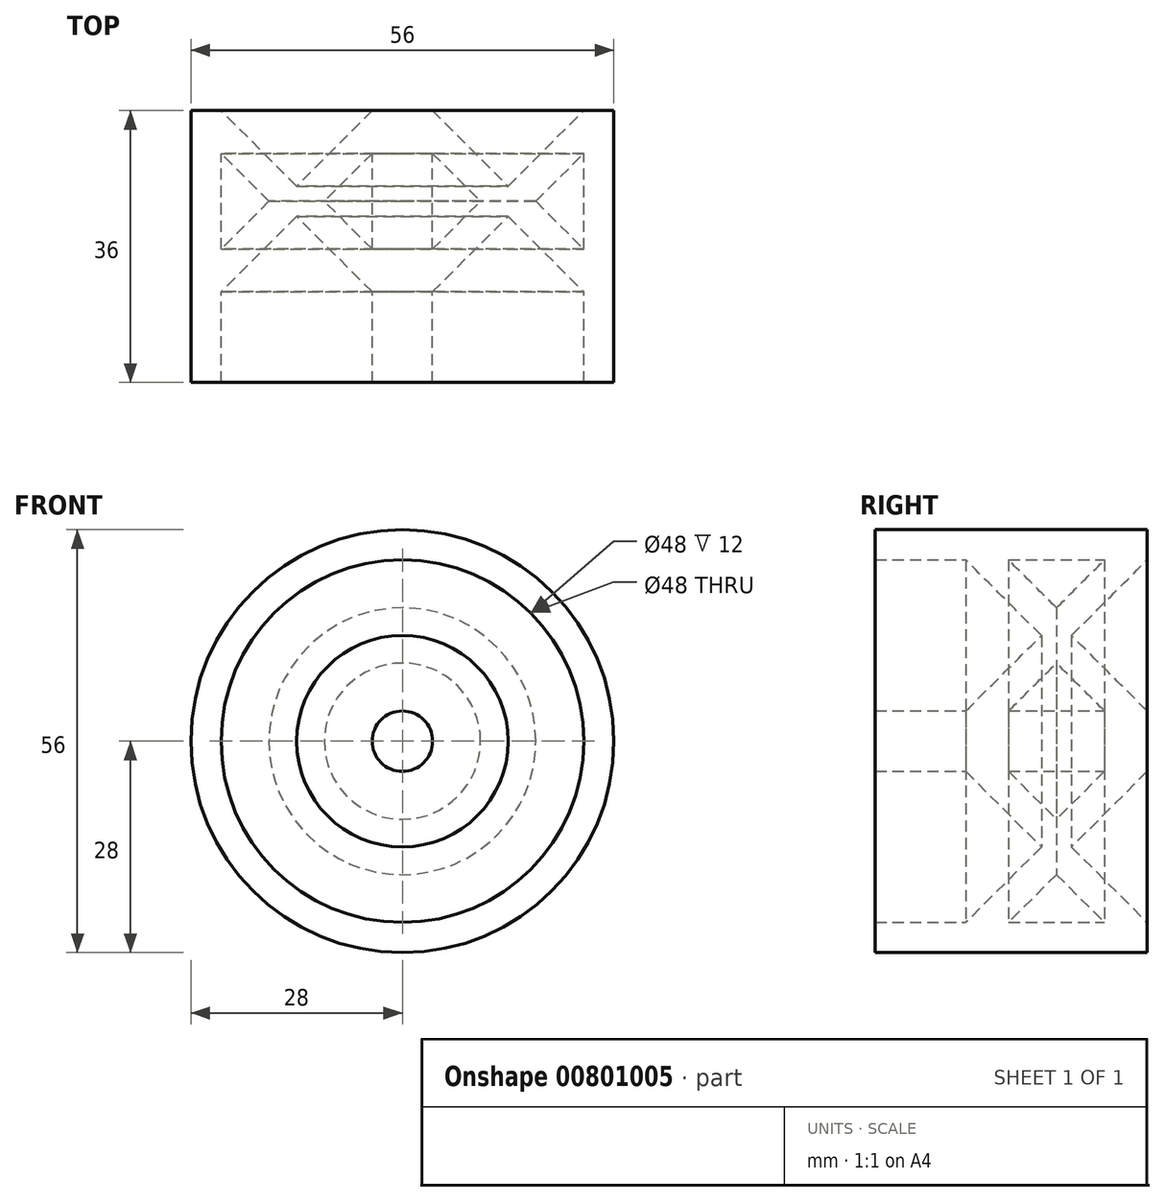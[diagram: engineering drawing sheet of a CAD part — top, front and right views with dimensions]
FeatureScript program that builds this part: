
annotation { "Feature Type Name" : "Feature", "Feature Type Description" : "" }
export const myFeature = defineFeature(function(context is Context, id is Id, definition is map)
    precondition{}
    {
        {
            var Q0;
            Q0=qCreatedBy(makeId("Top.planeOp"),FACE);
            var sketch = newSketch(context, id + "F0", { "sketchPlane" : qUnion([Q0])});
            skLineSegment(sketch, "E0", {"start": v(4, -24) * mm, "end": v(14, -14) * mm});
            skLineSegment(sketch, "E1", {"start": v(14, -14) * mm, "end": v(24, -24) * mm});
            skLineSegment(sketch, "E2", {"start": v(28, 0) * mm, "end": v(24, 0) * mm});
            skLineSegment(sketch, "E3", {"start": v(24, 0) * mm, "end": v(14, -10) * mm});
            skLineSegment(sketch, "E4", {"start": v(14, -10) * mm, "end": v(4, 0) * mm});
            skLineSegment(sketch, "E5", {"start": v(4, 0) * mm, "end": v(0, 0) * mm});
            skLineSegment(sketch, "E6", {"start": v(4, -18.34) * mm, "end": v(10.34, -12) * mm});
            skLineSegment(sketch, "E7", {"start": v(10.34, -12) * mm, "end": v(4, -5.66) * mm});
            skLineSegment(sketch, "E8", {"start": v(4, -5.66) * mm, "end": v(4, -18.34) * mm});
            skLineSegment(sketch, "E9", {"start": v(14, -10) * mm, "end": v(14, -14) * mm, "construction": true});
            skLineSegment(sketch, "E10.MirrorCS", {"start": v(17.66, -12) * mm, "end": v(24, -5.66) * mm});
            skLineSegment(sketch, "E11.MirrorCS", {"start": v(24, -5.66) * mm, "end": v(24, -18.34) * mm});
            skLineSegment(sketch, "E12.MirrorCS", {"start": v(24, -18.34) * mm, "end": v(17.66, -12) * mm});
            skLineSegment(sketch, "E13", {"start": v(0, -36) * mm, "end": v(4, -36) * mm});
            skLineSegment(sketch, "E14", {"start": v(4, -36) * mm, "end": v(4, -24) * mm});
            skLineSegment(sketch, "E15", {"start": v(24, -24) * mm, "end": v(24, -36) * mm});
            skLineSegment(sketch, "E16", {"start": v(24, -36) * mm, "end": v(28, -36) * mm});
            skLineSegment(sketch, "E17", {"start": v(28, -36) * mm, "end": v(28, 0) * mm});
            skLineSegment(sketch, "E18", {"start": v(0, 0) * mm, "end": v(0, -36) * mm});
            skSolve(sketch);
        }
        {
            var Q0;
            Q0=makeQuery(id+"F0.imprint","IMPRINT",FACE,{"disambiguationData":[TD([[makeQuery(id+"F0.imprint","IMPRINT",EDGE,{"derivedFrom":sQuery(id+"F0.wireOp",EDGE,"E0")}),1.0]])]});
            var Q1;
            Q1=sQuery(id+"F0.wireOp",EDGE,"E18");
            revolve(context, id + "F1", {"surfaceOperationType" : NewSurfaceOperationType.NEW, "entities" : qUnion([Q0]), "axis" : qUnion([Q1]), "revolveType" : RevolveType.FULL});
        }
    });
